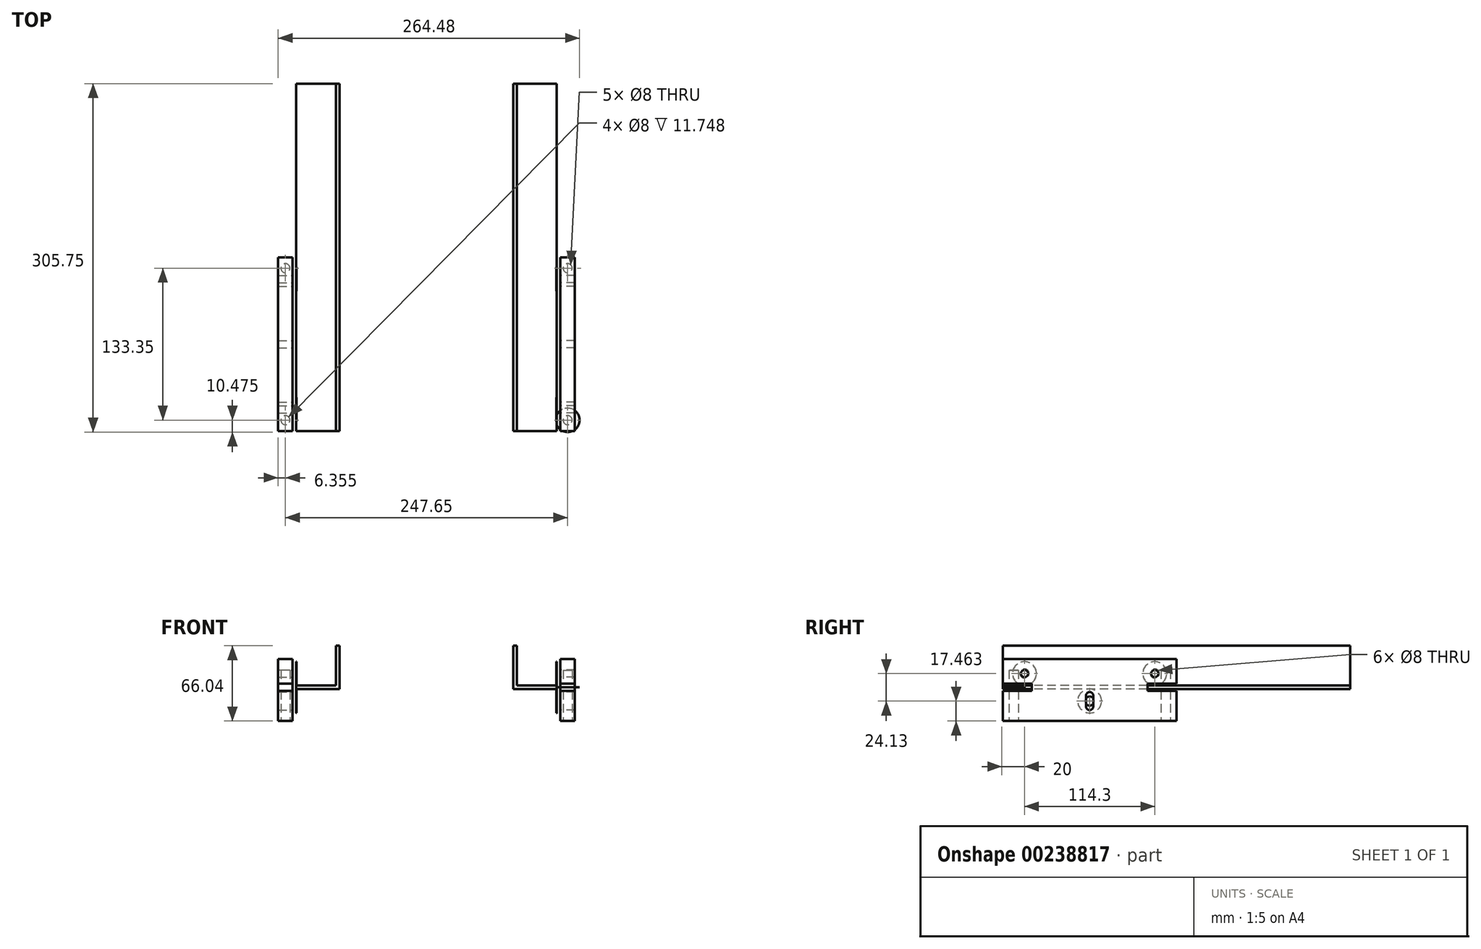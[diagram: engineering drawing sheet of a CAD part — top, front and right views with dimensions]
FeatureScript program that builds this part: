
annotation { "Feature Type Name" : "Feature", "Feature Type Description" : "" }
export const myFeature = defineFeature(function(context is Context, id is Id, definition is map)
    precondition{}
    {
        {
            assignVariable(context, id + "F0", {"name" : "bearingT", "anyValue" : .275});
        }
        {
            var Q0;
            Q0=qCreatedBy(makeId("Front.planeOp"),FACE);
            var sketch = newSketch(context, id + "F1", { "sketchPlane" : qUnion([Q0])});
            skLineSegment(sketch, "E0", {"start": v(76.2, 38.1) * mm, "end": v(76.2, 0) * mm});
            skLineSegment(sketch, "E1", {"start": v(76.2, 0) * mm, "end": v(114.3, 0) * mm});
            skLineSegment(sketch, "E2", {"start": v(114.3, 0) * mm, "end": v(114.3, 3.18) * mm});
            skLineSegment(sketch, "E3", {"start": v(114.3, 3.18) * mm, "end": v(79.38, 3.18) * mm});
            skLineSegment(sketch, "E4", {"start": v(79.38, 3.18) * mm, "end": v(79.38, 38.1) * mm});
            skLineSegment(sketch, "E5", {"start": v(79.38, 38.1) * mm, "end": v(76.2, 38.1) * mm});
            skLineSegment(sketch, "E6.MirrorCS", {"start": v(-79.38, 38.1) * mm, "end": v(-76.2, 38.1) * mm});
            skLineSegment(sketch, "E7.MirrorCS", {"start": v(-114.3, 0) * mm, "end": v(-114.3, 3.18) * mm});
            skLineSegment(sketch, "E8.MirrorCS", {"start": v(-79.38, 3.18) * mm, "end": v(-79.38, 38.1) * mm});
            skLineSegment(sketch, "E9.MirrorCS", {"start": v(-76.2, 38.1) * mm, "end": v(-76.2, 0) * mm});
            skLineSegment(sketch, "E10.MirrorCS", {"start": v(-114.3, 3.18) * mm, "end": v(-79.38, 3.18) * mm});
            skLineSegment(sketch, "E11.MirrorCS", {"start": v(-76.2, 0) * mm, "end": v(-114.3, 0) * mm});
            skPoint(sketch, "E12", {"position": v(114.3, 1.59) * mm});
            skPoint(sketch, "E13", {"position": v(77.79, 38.1) * mm});
            skSolve(sketch);
        }
        {
            var Q0;
            Q0 = qSketchRegion(id + "F1", true);
            extrude(context, id + "F2", {"entities" : qUnion([Q0]), "oppositeDirection" : true, "depth" : 304.8 * mm});
        }
        {
            var Q0;
            Q0=makeQuery(id+"F2.opExtrude","SWEPT_FACE",FACE,{"disambiguationData":[OSD([sQuery(id+"F1.wireOp",EDGE,"E2")])]});
            cPlane(context, id + "F3", {"entities" : qUnion([Q0]), "cplaneType" : CPlaneType.OFFSET, "offset" : 3.17 * mm, "width" : 152.4 * mm, "height" : 152.4 * mm});
        }
        {
            var Q0;
            Q0=qCreatedBy(id+"F3.planeOp",FACE);
            var sketch = newSketch(context, id + "F4", { "sketchPlane" : qUnion([Q0])});
            skLineSegment(sketch, "E14", {"start": v(0, 26.35) * mm, "end": v(0, -27.94) * mm});
            skLineSegment(sketch, "E15", {"start": v(0, -27.94) * mm, "end": v(152.4, -27.94) * mm});
            skLineSegment(sketch, "E16", {"start": v(152.4, 26.35) * mm, "end": v(0, 26.35) * mm});
            skLineSegment(sketch, "E17", {"start": v(0, 13.65) * mm, "end": v(152.4, 13.65) * mm, "construction": true});
            skLineSegment(sketch, "E18", {"start": v(0, -10.48) * mm, "end": v(152.4, -10.48) * mm, "construction": true});
            skPoint(sketch, "E19", {"position": v(76.2, -27.94) * mm});
            skLineSegment(sketch, "E20", {"start": v(76.2, -15.24) * mm, "end": v(76.2, -5.72) * mm, "construction": true});
            skArc(sketch, "E21.0.startCap", {"start": v(79.38, -15.24) * mm, "mid": v(76.2, -18.41) * mm, "end": v(73.03, -15.24) * mm});
            skArc(sketch, "E21.0.endCap", {"start": v(73.03, -5.72) * mm, "mid": v(76.2, -2.54) * mm, "end": v(79.38, -5.72) * mm});
            skLineSegment(sketch, "E21.0.left", {"start": v(73.03, -15.24) * mm, "end": v(73.03, -5.72) * mm});
            skLineSegment(sketch, "E21.0.right", {"start": v(79.38, -15.24) * mm, "end": v(79.38, -5.72) * mm});
            skPoint(sketch, "E22", {"position": v(76.2, -10.48) * mm});
            skLineSegment(sketch, "E23", {"start": v(152.4, 26.35) * mm, "end": v(152.4, -27.94) * mm});
            skCircle(sketch, "E24", {"center": v(19.05, 13.65) * mm, "radius": 3.18 * mm});
            skPoint(sketch, "E25", {"position": v(76.2, 26.35) * mm});
            skLineSegment(sketch, "E26", {"start": v(76.2, 26.35) * mm, "end": v(76.2, -27.94) * mm, "construction": true});
            skLineSegment(sketch, "E27", {"start": v(19.05, 26.35) * mm, "end": v(19.05, -27.94) * mm, "construction": true});
            skCircle(sketch, "E28", {"center": v(133.35, 13.65) * mm, "radius": 3.18 * mm});
            skLineSegment(sketch, "E29.MirrorCS", {"start": v(133.35, 26.35) * mm, "end": v(133.35, -27.94) * mm, "construction": true});
            skLineSegment(sketch, "E30", {"start": v(0, 3.56) * mm, "end": v(152.4, 3.56) * mm, "construction": true});
            skLineSegment(sketch, "E31", {"start": v(0, 3.18) * mm, "end": v(0, 0) * mm, "construction": true});
            skPoint(sketch, "E32", {"position": v(0, 1.59) * mm});
            skLineSegment(sketch, "E33.bottom", {"start": v(0, -1.59) * mm, "end": v(25.4, -1.59) * mm});
            skLineSegment(sketch, "E33.top", {"start": v(0, 4.76) * mm, "end": v(25.4, 4.76) * mm});
            skLineSegment(sketch, "E33.left", {"start": v(0, 4.76) * mm, "end": v(0, -1.59) * mm});
            skLineSegment(sketch, "E33.right", {"start": v(25.4, 4.76) * mm, "end": v(25.4, -1.59) * mm});
            skLineSegment(sketch, "E34.MirrorCS", {"start": v(127, 4.76) * mm, "end": v(127, -1.59) * mm});
            skLineSegment(sketch, "E35.MirrorCS", {"start": v(152.4, 4.76) * mm, "end": v(127, 4.76) * mm});
            skLineSegment(sketch, "E36.MirrorCS", {"start": v(152.4, -1.59) * mm, "end": v(127, -1.59) * mm});
            skLineSegment(sketch, "E37.MirrorCS", {"start": v(152.4, 4.76) * mm, "end": v(152.4, -1.59) * mm});
            skSolve(sketch);
        }
        {
            var Q0;
            {var subQ0=sQuery(id+"F4.wireOp",EDGE,"E15");Q0=makeQuery(id+"F4.imprint","IMPRINT",FACE,{"disambiguationData":[TD([[makeQuery(id+"F4.imprint","IMPRINT",EDGE,{"derivedFrom":subQ0}),1.0]])]});}
            extrude(context, id + "F5", {"entities" : qUnion([Q0]), "depth" : 12.7 * mm});
        }
        {
            var Q0;
            Q0=makeQuery(id+"F5.opExtrude","SWEPT_FACE",FACE,{"disambiguationData":[OSD([sQuery(id+"F4.wireOp",EDGE,"E15")])]});
            var sketch = newSketch(context, id + "F6", { "sketchPlane" : qUnion([Q0])});
            skLineSegment(sketch, "E38", {"start": v(130.18, 0) * mm, "end": v(117.48, 0) * mm, "construction": true});
            skLineSegment(sketch, "E39", {"start": v(130.18, -152.4) * mm, "end": v(117.48, -152.4) * mm, "construction": true});
            skLineSegment(sketch, "E40", {"start": v(123.83, 0) * mm, "end": v(123.83, -152.4) * mm, "construction": true});
            skPoint(sketch, "E41", {"position": v(123.83, -76.2) * mm});
            skLineSegment(sketch, "E42", {"start": v(130.18, -76.2) * mm, "end": v(117.48, -76.2) * mm});
            skCircle(sketch, "E43", {"center": v(123.83, -9.53) * mm, "radius": 4 * mm});
            skCircle(sketch, "E44.MirrorC", {"center": v(123.83, -142.88) * mm, "radius": 4 * mm});
            skSolve(sketch);
        }
        {
            var Q0;
            Q0 = qSketchRegion(id + "F6", true);
            extrude(context, id + "F7", {"entities" : qUnion([Q0]), "operationType" : NewBodyOperationType.REMOVE, "oppositeDirection" : true, "depth" : 44.45 * mm});
        }
        {
            var Q0;
            Q0=makeQuery(id+"F2.opExtrude","SWEPT_FACE",FACE,{"disambiguationData":[OSD([sQuery(id+"F1.wireOp",EDGE,"E2")])]});
            var sketch = newSketch(context, id + "F8", { "sketchPlane" : qUnion([Q0])});
            skCircle(sketch, "E45", {"center": v(19.05, 13.65) * mm, "radius": 4 * mm});
            skCircle(sketch, "E46", {"center": v(19.05, 13.65) * mm, "radius": 10.48 * mm});
            skCircle(sketch, "E47", {"center": v(133.35, 13.65) * mm, "radius": 4 * mm});
            skCircle(sketch, "E48", {"center": v(133.35, 13.65) * mm, "radius": 10.48 * mm});
            skCircle(sketch, "E49", {"center": v(76.2, -10.48) * mm, "radius": 4 * mm});
            skCircle(sketch, "E50", {"center": v(76.2, -10.48) * mm, "radius": 10.48 * mm});
            skSolve(sketch);
        }
        {
            var Q0;
            Q0 = qSketchRegion(id + "F8", true);
            extrude(context, id + "F9", {"entities" : qUnion([Q0]), "operationType" : NewBodyOperationType.ADD, "oppositeDirection" : true, "depth" : (getVariable(context, 'bearingT')) * mm});
        }
        {
            var Q0;
            Q0=makeQuery(id+"F2.opExtrude","SWEPT_BODY",BODY,{"disambiguationData":[OSD([sQuery(id+"F1.wireOp",EDGE,"E0"),sQuery(id+"F1.wireOp",EDGE,"E1"),sQuery(id+"F1.wireOp",EDGE,"E2"),sQuery(id+"F1.wireOp",EDGE,"E3"),sQuery(id+"F1.wireOp",EDGE,"E4"),sQuery(id+"F1.wireOp",EDGE,"E5")])]});
            var Q1;
            Q1=makeQuery(id+"F5.opExtrude","SWEPT_BODY",BODY,{"disambiguationData":[OSD([sQuery(id+"F4.wireOp",EDGE,"E14"),sQuery(id+"F4.wireOp",EDGE,"E15"),sQuery(id+"F4.wireOp",EDGE,"E16"),sQuery(id+"F4.wireOp",EDGE,"E21.0.startCap"),sQuery(id+"F4.wireOp",EDGE,"E21.0.endCap"),sQuery(id+"F4.wireOp",EDGE,"E21.0.left"),sQuery(id+"F4.wireOp",EDGE,"E21.0.right"),sQuery(id+"F4.wireOp",EDGE,"E23"),sQuery(id+"F4.wireOp",EDGE,"E24"),sQuery(id+"F4.wireOp",EDGE,"E28"),sQuery(id+"F4.wireOp",EDGE,"E33.bottom"),sQuery(id+"F4.wireOp",EDGE,"E33.top"),sQuery(id+"F4.wireOp",EDGE,"E33.right"),sQuery(id+"F4.wireOp",EDGE,"E34.MirrorCS"),sQuery(id+"F4.wireOp",EDGE,"E35.MirrorCS"),sQuery(id+"F4.wireOp",EDGE,"E36.MirrorCS")])]});
            var Q2;
            Q2=makeQuery(id+"F9.opExtrude","SWEPT_BODY",BODY,{"disambiguationData":[OSD([sQuery(id+"F8.wireOp",EDGE,"E45"),sQuery(id+"F8.wireOp",EDGE,"E46")])]});
            var Q3;
            Q3=makeQuery(id+"F9.opExtrude","SWEPT_BODY",BODY,{"disambiguationData":[OSD([sQuery(id+"F8.wireOp",EDGE,"E47"),sQuery(id+"F8.wireOp",EDGE,"E48")])]});
            var Q4;
            Q4=makeQuery(id+"F9.opExtrude","SWEPT_BODY",BODY,{"disambiguationData":[OSD([sQuery(id+"F8.wireOp",EDGE,"E49"),sQuery(id+"F8.wireOp",EDGE,"E50")])]});
            var Q5;
            Q5=qCreatedBy(makeId("Right.planeOp"),FACE);
            mirror(context, id + "F10", {"entities" : qUnion([Q0, Q1, Q2, Q3, Q4]), "mirrorPlane" : qUnion([Q5])});
        }
        {
            var Q0;
            Q0=makeQuery(id+"F5.opExtrude","SWEPT_FACE",FACE,{"disambiguationData":[OSD([sQuery(id+"F4.wireOp",EDGE,"E15")])]});
            var sketch = newSketch(context, id + "F11", { "sketchPlane" : qUnion([Q0])});
            skLineSegment(sketch, "E51.bottom", {"start": v(-130.18, 0) * mm, "end": v(130.18, 0) * mm});
            skLineSegment(sketch, "E51.top", {"start": v(-130.18, -152.4) * mm, "end": v(130.18, -152.4) * mm});
            skLineSegment(sketch, "E51.left", {"start": v(-130.18, 0) * mm, "end": v(-130.18, -152.4) * mm});
            skLineSegment(sketch, "E51.right", {"start": v(130.18, 0) * mm, "end": v(130.18, -152.4) * mm});
            skSolve(sketch);
        }
        {
            var Q0;
            Q0=makeQuery(id+"F2.opExtrude","SWEPT_FACE",FACE,{"disambiguationData":[OSD([sQuery(id+"F1.wireOp",EDGE,"E3")])]});
            var Q1;
            Q1=sQuery(id+"F1.wireOp",VERTEX,"E12");
            cPlane(context, id + "F12", {"entities" : qUnion([Q0, Q1]), "cplaneType" : CPlaneType.PLANE_POINT, "offset" : 25.4 * mm, "width" : 152.4 * mm, "height" : 152.4 * mm});
        }
        {
            var Q0;
            Q0=qCreatedBy(id+"F12.planeOp",FACE);
            var sketch = newSketch(context, id + "F13", { "sketchPlane" : qUnion([Q0])});
            skCircle(sketch, "E52", {"center": v(123.83, 9.53) * mm, "radius": 4 * mm});
            skCircle(sketch, "E53", {"center": v(123.83, 9.53) * mm, "radius": 10.48 * mm});
            skSolve(sketch);
        }
        {
            var Q0;
            Q0 = qSketchRegion(id + "F13", true);
            extrude(context, id + "F14", {"entities" : qUnion([Q0]), "endBound" : BoundingType.SYMMETRIC, "depth" : getVariable(context, 'bearingT') / 50.8 * mm});
        }
    });
